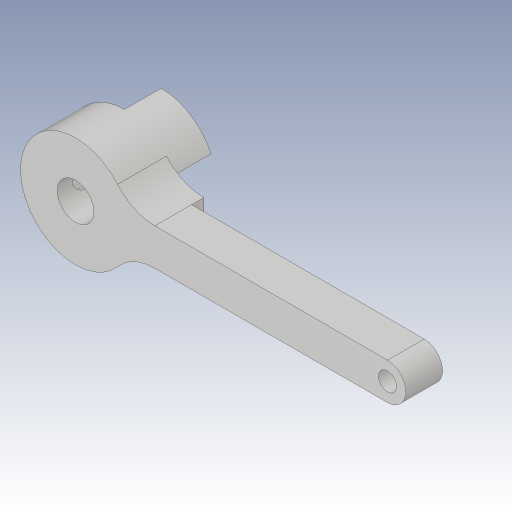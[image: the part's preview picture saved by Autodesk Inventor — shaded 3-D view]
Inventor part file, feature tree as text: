
AUTODESK INVENTOR PART (.ipt)
format: ipt  version: 2023.3 (Build 273359000, 359)  size: 195,584 bytes
history: native  units: in
note: dims shown in document units (in); Inventor stores cm internally (conversion verified against a paired STEP export)
features: sketch x4, extrude x3, fillet x2, hole x2, projected_geometry x2, plane x1
ambient origin geometry x8: Origin, YZ Plane, XZ Plane, XY Plane, X Axis, Y Axis, Z Axis, Center Point
bodies: Body1 (feature_tree)
feature tree (14):
  sketch  "Skizze3"  dims[d4=0.1181in d5=0.3543in d6=0.1181in]
  extrude  "Extrusion3"  Depth=0.1181in
  fillet  "Rundung1"  Radius=0.1181in
  plane  "Arbeitsebene1"
  hole  "Bohrung1"  [1 undecoded]
  extrude  "Extrusion4"  Depth=0.1181in TaperAngle=0.0deg
  hole  "Bohrung2"  [1 undecoded]
  fillet  "Rundung2"  Radius=0.0591in
  extrude  "Extrusion5"  Depth=0.0591in
  sketch  "Skizze4"  dims[d7=1.063in d8=0.1575in d9=0.0in]
  sketch  "Skizze5"  dims[d10=0.1575in]
  projected_geometry  "Projizierte Kontur1"
  sketch  "Skizze6"  dims[d11=0.0617in d12=0.1772in d13=0.2559in d14=0.0945in d15=90.0deg d16=0.1772in d17=0.0in d22=0.1181in d23=0.0in d24=0.1718in d25=0.0591in d26=0.0591in d27=0.1772in d28=0.1575in d29=0.0787in d30=90.0deg d31=0.1772in d32=0.0in d33=0.0591in d34=0.0394in d35=0.0in]
  projected_geometry  "Projizierte Kontur2"
note: 2 required parameter values undecoded (feature->parameter linkage not recoverable at this tier; creation-order binding heuristic only, values carry confidence <= 0.55)
